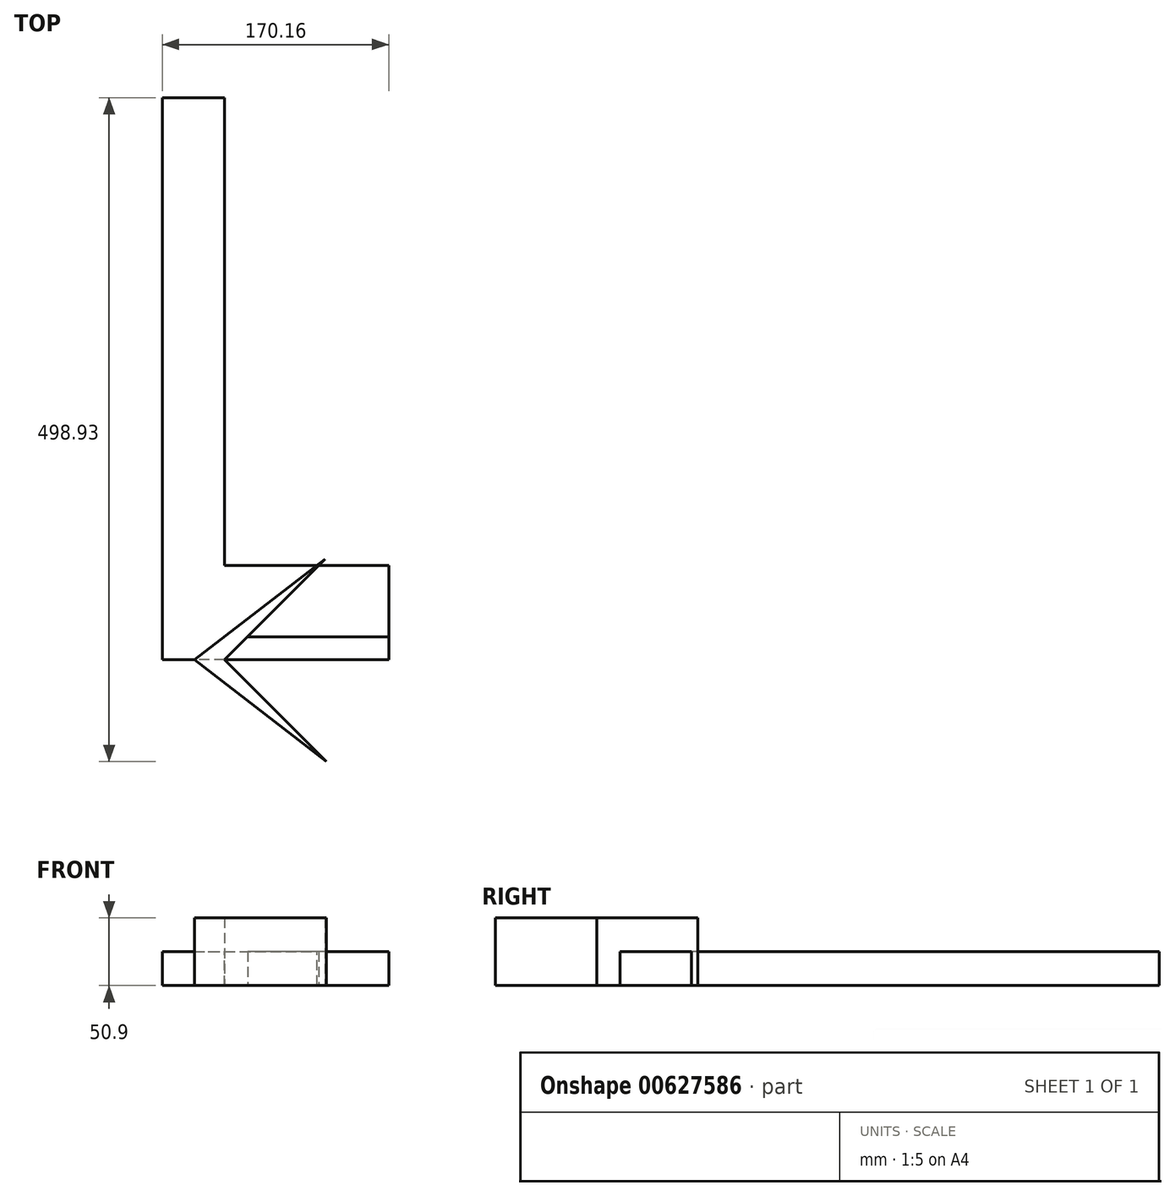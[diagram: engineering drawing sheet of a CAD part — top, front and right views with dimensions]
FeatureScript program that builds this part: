
annotation { "Feature Type Name" : "Feature", "Feature Type Description" : "" }
export const myFeature = defineFeature(function(context is Context, id is Id, definition is map)
    precondition{}
    {
        {
            var Q0;
            Q0=qCreatedBy(makeId("Top.planeOp"),FACE);
            var sketch = newSketch(context, id + "F0", { "sketchPlane" : qUnion([Q0])});
            skLineSegment(sketch, "E0", {"start": v(76.6, 75.59) * mm, "end": v(-46.75, 0) * mm});
            skLineSegment(sketch, "E1", {"start": v(-46.75, 0) * mm, "end": v(0, 0) * mm});
            skSolve(sketch);
        }
        {
            var Q0;
            Q0=qCreatedBy(makeId("Top.planeOp"),FACE);
            var sketch = newSketch(context, id + "F1", { "sketchPlane" : qUnion([Q0])});
            skLineSegment(sketch, "E2", {"start": v(-46.32, 0) * mm, "end": v(76.48, -76.43) * mm});
            skLineSegment(sketch, "E3", {"start": v(76.48, -76.43) * mm, "end": v(0, 0) * mm});
            skLineSegment(sketch, "E4", {"start": v(0, 0) * mm, "end": v(75.65, 75.7) * mm});
            skLineSegment(sketch, "E5", {"start": v(75.65, 75.7) * mm, "end": v(-22.48, 0) * mm});
            skLineSegment(sketch, "E6", {"start": v(-22.48, 0) * mm, "end": v(76.48, -76.43) * mm});
            skSolve(sketch);
        }
        {
            var Q0;
            Q0=makeQuery(id+"F1.imprint","IMPRINT",FACE,{"disambiguationData":[TD([[makeQuery(id+"F1.imprint","IMPRINT",EDGE,{"derivedFrom":sQuery(id+"F1.wireOp",EDGE,"E3")}),1.0]])]});
            extrude(context, id + "F2", {"entities" : qUnion([Q0]), "depth" : 25.4 * mm, "offsetDistance" : 25.4 * mm});
        }
        {
            var Q0;
            Q0=qCreatedBy(makeId("Top.planeOp"),FACE);
            var sketch = newSketch(context, id + "F3", { "sketchPlane" : qUnion([Q0])});
            skLineSegment(sketch, "E7", {"start": v(-46.98, 0) * mm, "end": v(77.37, -75.51) * mm});
            skSolve(sketch);
        }
        {
            var Q0;
            Q0=makeQuery(id+"F2.opExtrude","CAP_FACE",FACE,{"disambiguationData":[OSD([sQuery(id+"F1.wireOp",EDGE,"E3"),sQuery(id+"F1.wireOp",EDGE,"E4"),sQuery(id+"F1.wireOp",EDGE,"E5"),sQuery(id+"F1.wireOp",EDGE,"E6")])],"isStart":true});
            extrude(context, id + "F4", {"entities" : qUnion([Q0]), "operationType" : NewBodyOperationType.ADD, "depth" : 25.4 * mm, "offsetDistance" : 25.4 * mm});
        }
        {
            var Q0;
            Q0=sQuery(id+"F0.wireOp",EDGE,"E1");
            extrude(context, id + "F5", {"bodyType" : ToolBodyType.SURFACE, "surfaceEntities" : qUnion([Q0]), "oppositeDirection" : true, "depth" : 25.5 * mm, "offsetDistance" : 25.4 * mm});
        }
        {
            var Q0;
            Q0=sQuery(id+"F3.wireOp",EDGE,"E7");
            extrude(context, id + "F6", {"bodyType" : ToolBodyType.SURFACE, "surfaceEntities" : qUnion([Q0]), "depth" : 25.4 * mm, "offsetDistance" : 25.4 * mm});
        }
        {
            var Q0;
            Q0=qCreatedBy(makeId("Top.planeOp"),FACE);
            var sketch = newSketch(context, id + "F7", { "sketchPlane" : qUnion([Q0])});
            skLineSegment(sketch, "E8", {"start": v(-45.83, 0) * mm, "end": v(75.13, 74.79) * mm});
            skSolve(sketch);
        }
        {
            var Q0;
            Q0=sQuery(id+"F7.wireOp",EDGE,"E8");
            extrude(context, id + "F8", {"bodyType" : ToolBodyType.SURFACE, "surfaceEntities" : qUnion([Q0]), "depth" : 25.4 * mm, "offsetDistance" : 25.4 * mm});
        }
        {
            var Q0;
            Q0=makeQuery(id+"F5.opExtrude","SWEPT_FACE",FACE,{"disambiguationData":[OSD([sQuery(id+"F0.wireOp",EDGE,"E1")])]});
            extrude(context, id + "F9", {"entities" : qUnion([Q0]), "operationType" : NewBodyOperationType.ADD, "depth" : 70.9 * mm, "offsetDistance" : 25.4 * mm});
        }
        {
            var Q0;
            Q0=makeQuery(id+"F9.opExtrude","SWEPT_FACE",FACE,{"disambiguationData":[OSD([sQuery(id+"F0.wireOp",VERTEX,"E1.end")])]});
            extrude(context, id + "F10", {"entities" : qUnion([Q0]), "operationType" : NewBodyOperationType.ADD, "depth" : 123.4 * mm, "offsetDistance" : 25.4 * mm});
        }
        {
            var Q0;
            Q0=makeQuery(id+"F5.opExtrude","SWEPT_FACE",FACE,{"disambiguationData":[OSD([sQuery(id+"F0.wireOp",EDGE,"E1")])]});
            extrude(context, id + "F11", {"entities" : qUnion([Q0]), "operationType" : NewBodyOperationType.ADD, "depth" : 422.5 * mm, "offsetDistance" : 25.4 * mm});
        }
    });
